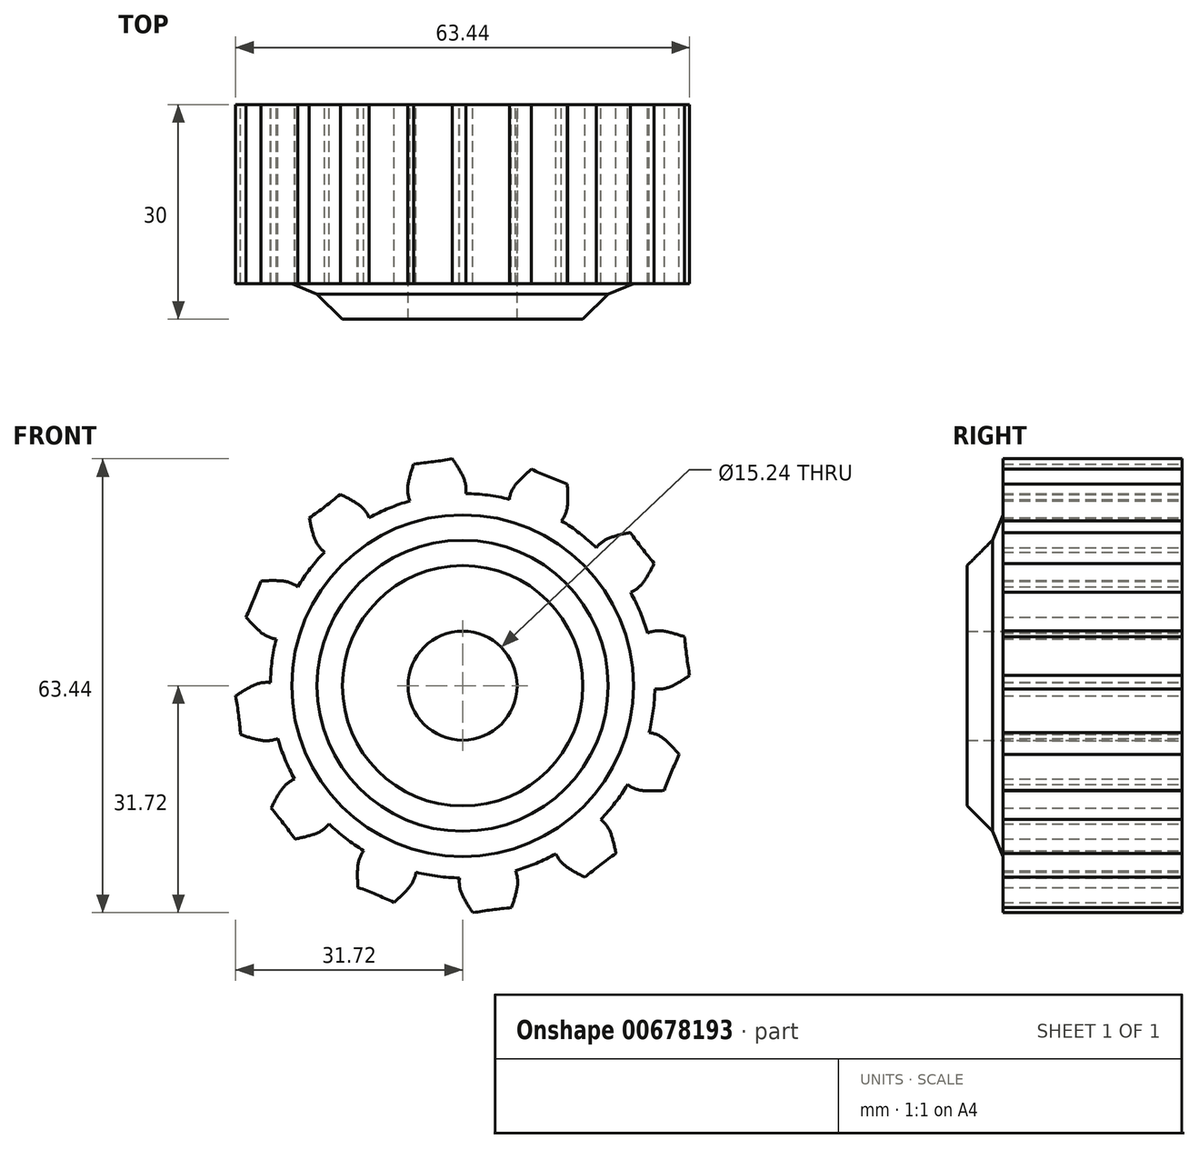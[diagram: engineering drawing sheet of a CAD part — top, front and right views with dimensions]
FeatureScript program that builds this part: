
annotation { "Feature Type Name" : "Feature", "Feature Type Description" : "" }
export const myFeature = defineFeature(function(context is Context, id is Id, definition is map)
    precondition{}
    {
        {
            var Q0;
            Q0=qCreatedBy(makeId("Front.planeOp"),FACE);
            var sketch = newSketch(context, id + "F0", { "sketchPlane" : qUnion([Q0])});
            skCircle(sketch, "E0", {"center": v(0, 0) * mm, "radius": 26.86 * mm});
            skCircle(sketch, "E1", {"center": v(0, 0) * mm, "radius": 29.34 * mm, "construction": true});
            skCircle(sketch, "E2", {"center": v(0, 0) * mm, "radius": 31.75 * mm, "construction": true});
            skLineSegment(sketch, "E3", {"start": v(0, 0) * mm, "end": v(0, 72.49) * mm, "construction": true});
            skLineSegment(sketch, "E4", {"start": v(0, 0) * mm, "end": v(-10.47, 79.5) * mm, "construction": true});
            skLineSegment(sketch, "E5", {"start": v(0, 29.34) * mm, "end": v(-56.45, 29.34) * mm, "construction": true});
            skLineSegment(sketch, "E6", {"start": v(0, 29.34) * mm, "end": v(-56.45, 8.8) * mm, "construction": true});
            skCircle(sketch, "E7", {"center": v(0, 0) * mm, "radius": 27.57 * mm, "construction": true});
            skCircle(sketch, "E8", {"center": v(0, 29.34) * mm, "radius": 7.3 * mm, "construction": true});
            skCircle(sketch, "E9", {"center": v(-6.86, 26.84) * mm, "radius": 7.3 * mm, "construction": true});
            skArc(sketch, "E10", {"start": v(0, 29.34) * mm, "mid": v(-0.67, 30.55) * mm, "end": v(-1.43, 31.72) * mm});
            skArc(sketch, "E11", {"start": v(0.44, 26.86) * mm, "mid": v(0.4, 28.13) * mm, "end": v(0, 29.34) * mm});
            skArc(sketch, "E12.MirrorCS", {"start": v(-7.6, 28.34) * mm, "mid": v(-7.26, 29.69) * mm, "end": v(-6.83, 31) * mm});
            skArc(sketch, "E13.MirrorCS", {"start": v(-7.38, 25.83) * mm, "mid": v(-7.67, 27.07) * mm, "end": v(-7.6, 28.34) * mm});
            skArc(sketch, "E14", {"start": v(-6.83, 31) * mm, "mid": v(-4.12, 31.3) * mm, "end": v(-1.43, 31.72) * mm});
            skCircle(sketch, "E15", {"center": v(0, 0) * mm, "radius": 21.8 * mm});
            skPoint(sketch, "E16.0.midPoint", {"position": v(10.58, -12.62) * mm});
            skCircle(sketch, "E17", {"center": v(0, 0) * mm, "radius": 7.62 * mm});
            skSolve(sketch);
        }
        {
            var Q0;
            {var subQ0=sQuery(id+"F0.wireOp",EDGE,"E0");var subQ1=makeQuery(id+"F0.imprint","INTERSECT",VERTEX,{"derivedFrom":[subQ0,sQuery(id+"F0.wireOp",EDGE,"E11")]});Q0=makeQuery(id+"F0.imprint","IMPRINT",FACE,{"disambiguationData":[TD([[makeQuery(id+"F0.imprint","IMPRINT",EDGE,{"disambiguationData":[TD([[subQ1,-1.0]])],"derivedFrom":subQ0}),1.0]])]});}
            var Q1;
            Q1=makeQuery(id+"F0.imprint","IMPRINT",FACE,{"disambiguationData":[TD([[makeQuery(id+"F0.imprint","IMPRINT",EDGE,{"derivedFrom":sQuery(id+"F0.wireOp",EDGE,"E10")}),1.0]])]});
            extrude(context, id + "F1", {"entities" : qUnion([Q0, Q1]), "depth" : 25 * mm, "offsetDistance" : 25 * mm});
        }
        {
            var Q0;
            Q0=makeQuery(id+"F1.opExtrude","SWEPT_BODY",BODY,{"disambiguationData":[OSD([sQuery(id+"F0.wireOp",EDGE,"E0"),sQuery(id+"F0.wireOp",EDGE,"E10"),sQuery(id+"F0.wireOp",EDGE,"E11"),sQuery(id+"F0.wireOp",EDGE,"E12.MirrorCS"),sQuery(id+"F0.wireOp",EDGE,"E13.MirrorCS"),sQuery(id+"F0.wireOp",EDGE,"E14")])]});
            var Q1;
            Q1=makeQuery(id+"F1.opExtrude","SWEPT_FACE",FACE,{"disambiguationData":[OSD([sQuery(id+"F0.wireOp",EDGE,"E0")])]});
            circularPattern(context, id + "F2", {"entities" : qUnion([Q0]), "axis" : qUnion([Q1]), "angle" : 360 * degree, "instanceCount" : 12, "equalSpace" : true});
        }
        {
            var Q0;
            Q0=makeQuery(id+"F0.imprint","IMPRINT",FACE,{"disambiguationData":[TD([[makeQuery(id+"F0.imprint","IMPRINT",EDGE,{"derivedFrom":sQuery(id+"F0.wireOp",EDGE,"E15")}),1.0]])]});
            extrude(context, id + "F3", {"entities" : qUnion([Q0]), "operationType" : NewBodyOperationType.ADD, "depth" : 30 * mm, "offsetDistance" : 25 * mm});
        }
        {
            var Q0;
            Q0=makeQuery(id+"F3.opExtrude","CAP_EDGE",EDGE,{"disambiguationData":[OSD([sQuery(id+"F0.wireOp",EDGE,"E15")])],"isStart":false});
            chamfer(context, id + "F4", {"entities" : qUnion([Q0]), "width" : 5 * mm, "tangentPropagation" : true});
        }
        {
            var Q0;
            {var subQ0=sQuery(id+"F0.wireOp",EDGE,"E15");var subQ1=makeQuery(id+"F1.opExtrude","CAP_FACE",FACE,{"disambiguationData":[OSD([sQuery(id+"F0.wireOp",EDGE,"E0"),sQuery(id+"F0.wireOp",EDGE,"E10"),sQuery(id+"F0.wireOp",EDGE,"E11"),sQuery(id+"F0.wireOp",EDGE,"E12.MirrorCS"),sQuery(id+"F0.wireOp",EDGE,"E13.MirrorCS"),sQuery(id+"F0.wireOp",EDGE,"E14"),subQ0])],"isStart":false});Q0=makeQuery(id+"F4.opChamfer","BLEND_EDGE",EDGE,{"blendedFrom":[makeQuery(id+"F3.opExtrude","CAP_EDGE",EDGE,{"disambiguationData":[OSD([subQ0])],"isStart":false}),makeQuery(id+"F3.boolean.opBoolean","MERGE",FACE,{"derivedFrom":[subQ1,makeQuery(id+"F2.opPattern","COPY",FACE,{"derivedFrom":subQ1,"instanceName":"1"}),makeQuery(id+"F2.opPattern","COPY",FACE,{"derivedFrom":subQ1,"instanceName":"2"}),makeQuery(id+"F2.opPattern","COPY",FACE,{"derivedFrom":subQ1,"instanceName":"3"}),makeQuery(id+"F2.opPattern","COPY",FACE,{"derivedFrom":subQ1,"instanceName":"4"}),makeQuery(id+"F2.opPattern","COPY",FACE,{"derivedFrom":subQ1,"instanceName":"5"}),makeQuery(id+"F2.opPattern","COPY",FACE,{"derivedFrom":subQ1,"instanceName":"6"}),makeQuery(id+"F2.opPattern","COPY",FACE,{"derivedFrom":subQ1,"instanceName":"7"}),makeQuery(id+"F2.opPattern","COPY",FACE,{"derivedFrom":subQ1,"instanceName":"8"}),makeQuery(id+"F2.opPattern","COPY",FACE,{"derivedFrom":subQ1,"instanceName":"9"}),makeQuery(id+"F2.opPattern","COPY",FACE,{"derivedFrom":subQ1,"instanceName":"10"}),makeQuery(id+"F2.opPattern","COPY",FACE,{"derivedFrom":subQ1,"instanceName":"11"})]})],"blendedInto":[makeQuery(id+"F3.boolean.opBoolean","MERGE",FACE,{"derivedFrom":[subQ1,makeQuery(id+"F2.opPattern","COPY",FACE,{"derivedFrom":subQ1,"instanceName":"1"}),makeQuery(id+"F2.opPattern","COPY",FACE,{"derivedFrom":subQ1,"instanceName":"2"}),makeQuery(id+"F2.opPattern","COPY",FACE,{"derivedFrom":subQ1,"instanceName":"3"}),makeQuery(id+"F2.opPattern","COPY",FACE,{"derivedFrom":subQ1,"instanceName":"4"}),makeQuery(id+"F2.opPattern","COPY",FACE,{"derivedFrom":subQ1,"instanceName":"5"}),makeQuery(id+"F2.opPattern","COPY",FACE,{"derivedFrom":subQ1,"instanceName":"6"}),makeQuery(id+"F2.opPattern","COPY",FACE,{"derivedFrom":subQ1,"instanceName":"7"}),makeQuery(id+"F2.opPattern","COPY",FACE,{"derivedFrom":subQ1,"instanceName":"8"}),makeQuery(id+"F2.opPattern","COPY",FACE,{"derivedFrom":subQ1,"instanceName":"9"}),makeQuery(id+"F2.opPattern","COPY",FACE,{"derivedFrom":subQ1,"instanceName":"10"}),makeQuery(id+"F2.opPattern","COPY",FACE,{"derivedFrom":subQ1,"instanceName":"11"})]})]});}
            chamfer(context, id + "F5", {"entities" : qUnion([Q0]), "width" : 5 * mm, "tangentPropagation" : true});
        }
    });
